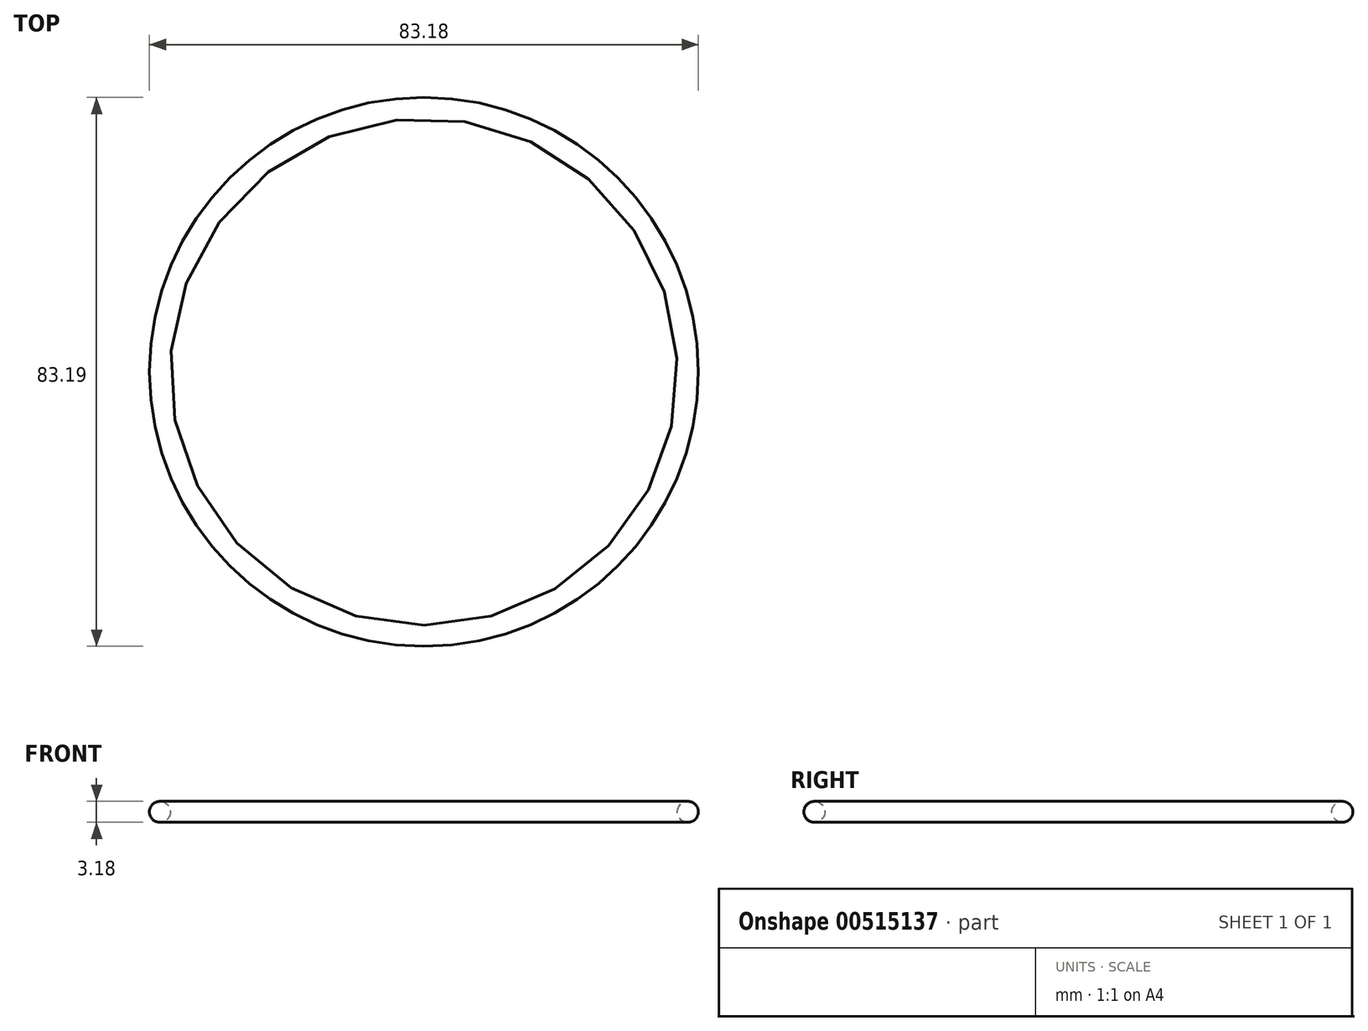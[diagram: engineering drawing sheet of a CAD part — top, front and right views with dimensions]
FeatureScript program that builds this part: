
annotation { "Feature Type Name" : "Feature", "Feature Type Description" : "" }
export const myFeature = defineFeature(function(context is Context, id is Id, definition is map)
    precondition{}
    {
        {
            var Q0;
            Q0=qCreatedBy(makeId("Right.planeOp"),FACE);
            var sketch = newSketch(context, id + "F0", { "sketchPlane" : qUnion([Q0])});
            skCircle(sketch, "E0", {"center": v(0, 0) * mm, "radius": 1.59 * mm});
            skSolve(sketch);
        }
        {
            var Q0;
            Q0=qCreatedBy(makeId("Top.planeOp"),FACE);
            var sketch = newSketch(context, id + "F1", { "sketchPlane" : qUnion([Q0])});
            skCircle(sketch, "E1", {"center": v(0.06, -40) * mm, "radius": 40 * mm});
            skPoint(sketch, "E1.first.point", {"position": v(0, 0) * mm});
            skPoint(sketch, "E1.second.point", {"position": v(0, -80) * mm});
            skPoint(sketch, "E1.third.point", {"position": v(-39.94, -39.89) * mm});
            skSolve(sketch);
        }
        {
            var Q0;
            Q0=makeQuery(id+"F0.imprint","IMPRINT",FACE,{"disambiguationData":[TD([[makeQuery(id+"F0.imprint","IMPRINT",EDGE,{"derivedFrom":sQuery(id+"F0.wireOp",EDGE,"E0")}),1.0]])]});
            var Q1;
            Q1=sQuery(id+"F1.wireOp",EDGE,"E1");
            sweep(context, id + "F2", {"profiles" : qUnion([Q0]), "path" : qUnion([Q1])});
        }
    });
